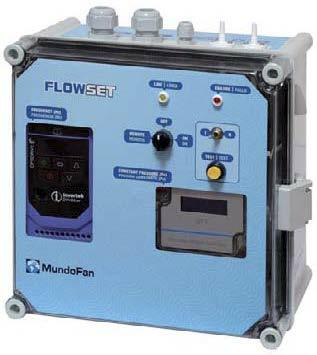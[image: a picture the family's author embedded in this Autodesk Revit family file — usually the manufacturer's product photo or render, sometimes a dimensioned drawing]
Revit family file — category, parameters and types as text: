
# Revit family: FLOWSET-4_VE10847
name_source: partatom
category: Aparatos eléctricos
revit_build: Autodesk Revit 2016 (Build: 20150220_1215(x64)
units: mm (PartAtom-declared; Revit-internal decimal feet)

## family parameters
Compartido = No
Corte con vacíos al cargar = No
Cota de conector redondo = Diámetro de uso
Mantener orientación de anotación = No
Número OmniClass = 23.80.00.00
Punto de cálculo de habitación = No
Se basa en plano de trabajo = No
Siempre vertical = Sí
Tipo de pieza = Caja de conexiones
Título OmniClass = Electric Power and Lighting

## types (1)
- FLOWSET
    Alimentación = 400Vac trifásico
    Corriente = 9,5 A
    Costo = 0 $
    Código de montaje = VE10847
    Descripción = CONTROL EFICIENCIA ENERGETICA PARA VENTILADORES - Caudal aire constante
    Dimensiones máx. = 270x300x170 mm
    Fabricante = SALVADOR ESCODA
    Imagen de tipo = flowset.jpg
    Leds = linea / fallo
    Modelo = FLOWSET 4kW
    Normativas = EN-ISO 14644-1:2000
    Potencia = 4 kW
    Regulación = Mediante sonda analógica de presión
    Salida = 400Vac trifásico
    Selector = 3 posiciones remoto / off / on
    URL = www.salvadorescoda.com
    Visualización = frecuencia (Hz) y presión (Pa)
